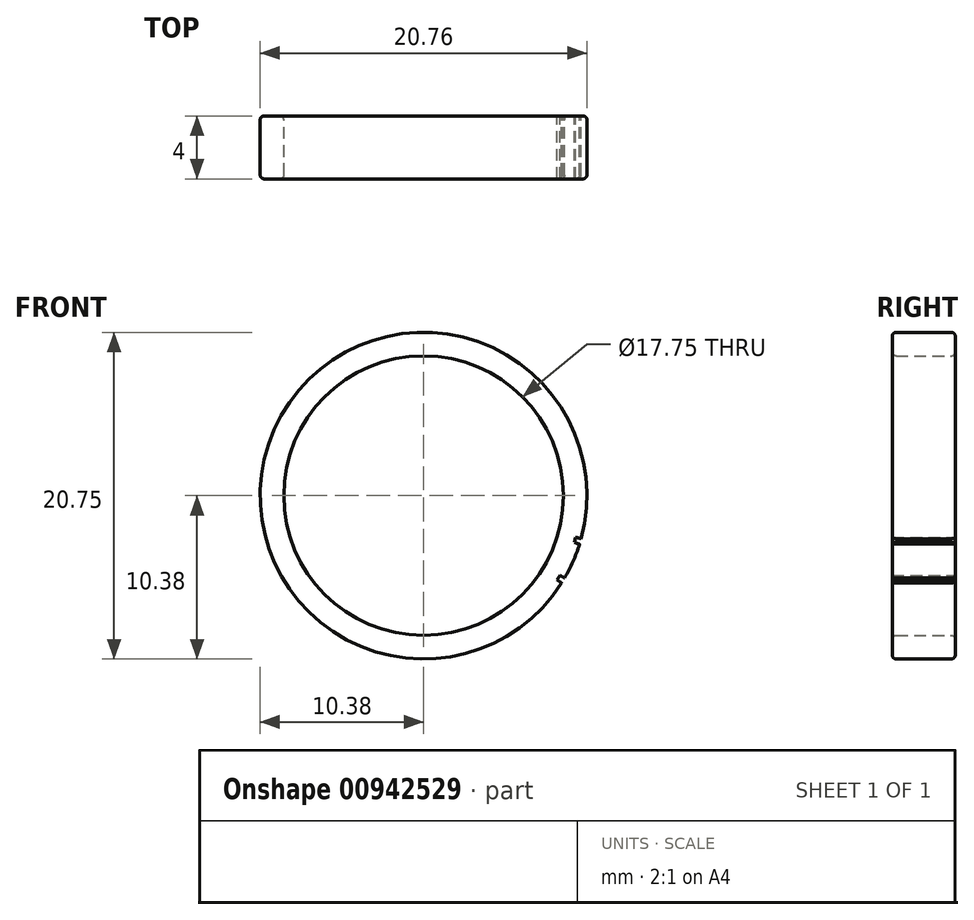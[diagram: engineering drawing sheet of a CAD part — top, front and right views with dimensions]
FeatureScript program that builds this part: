
annotation { "Feature Type Name" : "Feature", "Feature Type Description" : "" }
export const myFeature = defineFeature(function(context is Context, id is Id, definition is map)
    precondition{}
    {
        {
            var Q0;
            Q0=qCreatedBy(makeId("Front.planeOp"),FACE);
            var sketch = newSketch(context, id + "F0", { "sketchPlane" : qUnion([Q0])});
            skCircle(sketch, "E0", {"center": v(0, 0) * mm, "radius": 8.88 * mm});
            skCircle(sketch, "E1.0", {"center": v(0, 0) * mm, "radius": 10.38 * mm});
            skLineSegment(sketch, "E2", {"start": v(0, 0) * mm, "end": v(5.9, -8.53) * mm, "construction": true});
            skLineSegment(sketch, "E3", {"start": v(0, 0) * mm, "end": v(5.6, -8.73) * mm, "construction": true});
            skLineSegment(sketch, "E4", {"start": v(8.77, -5.54) * mm, "end": v(8.47, -5.36) * mm});
            skLineSegment(sketch, "E5", {"start": v(7.37, 6.8) * mm, "end": v(7.12, 7.05) * mm});
            skLineSegment(sketch, "E6", {"start": v(8.96, -5.23) * mm, "end": v(8.65, -5.05) * mm});
            skLineSegment(sketch, "E7", {"start": v(8.47, -5.36) * mm, "end": v(8.65, -5.05) * mm});
            skLineSegment(sketch, "E8", {"start": v(9.9, -3.09) * mm, "end": v(9.57, -2.98) * mm});
            skLineSegment(sketch, "E9", {"start": v(9.66, -2.64) * mm, "end": v(10, -2.74) * mm});
            skLineSegment(sketch, "E10", {"start": v(9.57, -2.98) * mm, "end": v(9.66, -2.64) * mm});
            skLineSegment(sketch, "E11", {"start": v(10.3, -1.32) * mm, "end": v(9.94, -1.27) * mm});
            skLineSegment(sketch, "E12", {"start": v(9.98, -0.93) * mm, "end": v(10.33, -0.96) * mm});
            skLineSegment(sketch, "E13", {"start": v(9.94, -1.27) * mm, "end": v(9.98, -0.93) * mm});
            skLineSegment(sketch, "E14", {"start": v(10.12, 2.28) * mm, "end": v(9.78, 2.2) * mm});
            skLineSegment(sketch, "E15", {"start": v(9.7, 2.54) * mm, "end": v(10.04, 2.63) * mm});
            skLineSegment(sketch, "E16", {"start": v(9.78, 2.2) * mm, "end": v(9.7, 2.54) * mm});
            skLineSegment(sketch, "E17", {"start": v(7.62, 7.04) * mm, "end": v(7.37, 6.8) * mm});
            skLineSegment(sketch, "E18", {"start": v(5.42, -8.44) * mm, "end": v(5.7, -8.24) * mm});
            skLineSegment(sketch, "E19", {"start": v(7.12, 7.05) * mm, "end": v(7.37, 7.3) * mm});
            skLineSegment(sketch, "E20", {"start": v(5.6, -8.73) * mm, "end": v(5.42, -8.44) * mm});
            skLineSegment(sketch, "E21", {"start": v(5.7, -8.24) * mm, "end": v(5.9, -8.53) * mm});
            skSolve(sketch);
        }
        {
            var Q0;
            Q0=makeQuery(id+"F0.imprint","IMPRINT",FACE,{"disambiguationData":[TD([[makeQuery(id+"F0.imprint","IMPRINT",EDGE,{"derivedFrom":sQuery(id+"F0.wireOp",EDGE,"E0")}),-1.0]])]});
            extrude(context, id + "F1", {"entities" : qUnion([Q0]), "depth" : 2 * mm, "offsetDistance" : 25 * mm, "hasSecondDirection" : true, "secondDirectionOppositeDirection" : true, "secondDirectionDepth" : 2 * mm});
        }
        {
            var Q0;
            Q0=makeQuery(id+"F1.opExtrude","CAP_EDGE",EDGE,{"disambiguationData":[OSD([sQuery(id+"F0.wireOp",EDGE,"E1.0")])],"isStart":true});
            var Q1;
            Q1=makeQuery(id+"F1.opExtrude","CAP_EDGE",EDGE,{"disambiguationData":[OSD([sQuery(id+"F0.wireOp",EDGE,"E1.0")])],"isStart":false});
            var Q2;
            Q2=makeQuery(id+"F1.opExtrude","CAP_EDGE",EDGE,{"disambiguationData":[OSD([sQuery(id+"F0.wireOp",EDGE,"E0")])],"isStart":false});
            var Q3;
            Q3=makeQuery(id+"F1.opExtrude","CAP_EDGE",EDGE,{"disambiguationData":[OSD([sQuery(id+"F0.wireOp",EDGE,"E0")])],"isStart":true});
            fillet(context, id + "F2", {"entities" : qUnion([Q0, Q1, Q2, Q3]), "tangentPropagation" : true, "radius" : .25 * mm, "defaultsChanged" : true, "vertexSettings" : [], "allowEdgeOverflow" : false});
        }
    });
